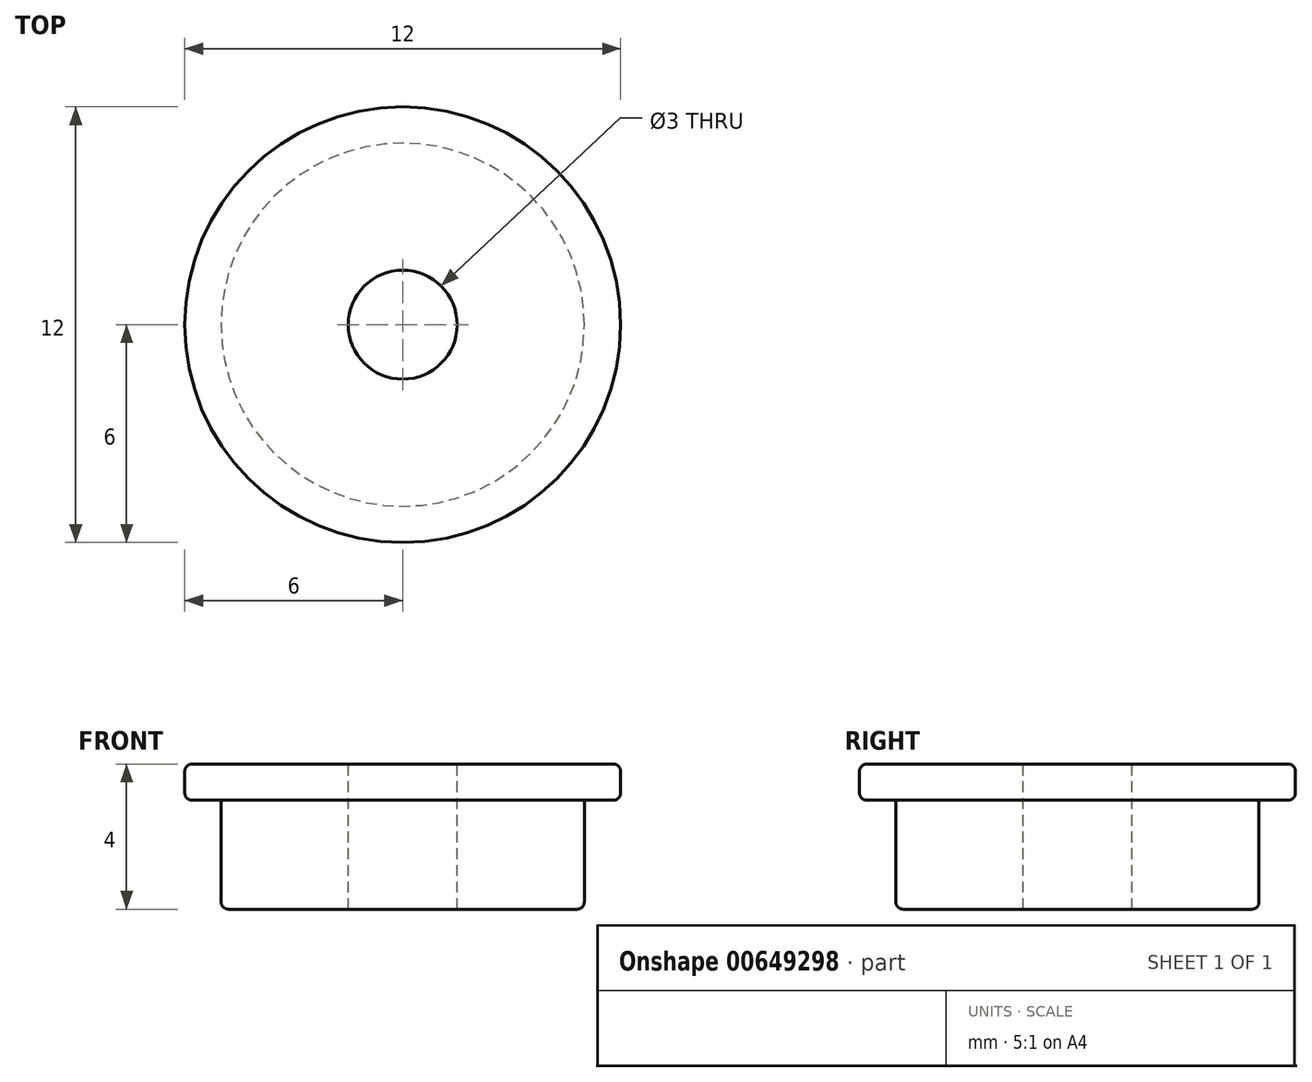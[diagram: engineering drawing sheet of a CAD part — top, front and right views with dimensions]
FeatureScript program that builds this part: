
annotation { "Feature Type Name" : "Feature", "Feature Type Description" : "" }
export const myFeature = defineFeature(function(context is Context, id is Id, definition is map)
    precondition{}
    {
        {
            var Q0;
            Q0=qCreatedBy(makeId("Front.planeOp"),FACE);
            var sketch = newSketch(context, id + "F0", { "sketchPlane" : qUnion([Q0])});
            skLineSegment(sketch, "E0", {"start": v(0, 0) * mm, "end": v(0, 4) * mm});
            skLineSegment(sketch, "E1", {"start": v(0, 4) * mm, "end": v(-5.8, 4) * mm});
            skLineSegment(sketch, "E2", {"start": v(-6, 3.8) * mm, "end": v(-6, 3.2) * mm});
            skLineSegment(sketch, "E3", {"start": v(-5.8, 3) * mm, "end": v(-5, 3) * mm});
            skLineSegment(sketch, "E4", {"start": v(-5, 3) * mm, "end": v(-5, 0.2) * mm});
            skLineSegment(sketch, "E5", {"start": v(-4.8, 0) * mm, "end": v(0, 0) * mm});
            skLineSegment(sketch, "E6", {"start": v(-1.5, 4) * mm, "end": v(-1.5, 0) * mm});
            skPoint(sketch, "E7.visualSharp", {"position": v(-5, 0) * mm});
            skArc(sketch, "E7.filletArc", {"start": v(-5, 0.2) * mm, "mid": v(-4.94, 0.06) * mm, "end": v(-4.8, 0) * mm});
            skPoint(sketch, "E8.visualSharp", {"position": v(-6, 3) * mm});
            skArc(sketch, "E8.filletArc", {"start": v(-6, 3.2) * mm, "mid": v(-5.94, 3.06) * mm, "end": v(-5.8, 3) * mm});
            skPoint(sketch, "E9.visualSharp", {"position": v(-6, 4) * mm});
            skArc(sketch, "E9.filletArc", {"start": v(-5.8, 4) * mm, "mid": v(-5.94, 3.94) * mm, "end": v(-6, 3.8) * mm});
            skArc(sketch, "E10.MirrorCS", {"start": v(-5, -0.2) * mm, "mid": v(-4.94, -0.06) * mm, "end": v(-4.8, 0) * mm});
            skArc(sketch, "E11.MirrorCS", {"start": v(-5.8, -4) * mm, "mid": v(-5.94, -3.94) * mm, "end": v(-6, -3.8) * mm});
            skArc(sketch, "E12.MirrorCS", {"start": v(-6, -3.2) * mm, "mid": v(-5.94, -3.06) * mm, "end": v(-5.8, -3) * mm});
            skPoint(sketch, "E13.MirrorP", {"position": v(-6, -4) * mm});
            skLineSegment(sketch, "E14.MirrorCS", {"start": v(0, 0) * mm, "end": v(0, -4) * mm});
            skPoint(sketch, "E15.MirrorP", {"position": v(-6, -3) * mm});
            skLineSegment(sketch, "E16.MirrorCS", {"start": v(0, -4) * mm, "end": v(-5.8, -4) * mm});
            skLineSegment(sketch, "E17.MirrorCS", {"start": v(-6, -3.8) * mm, "end": v(-6, -3.2) * mm});
            skLineSegment(sketch, "E18.MirrorCS", {"start": v(-5.8, -3) * mm, "end": v(-5, -3) * mm});
            skLineSegment(sketch, "E19.MirrorCS", {"start": v(-5, -3) * mm, "end": v(-5, -0.2) * mm});
            skLineSegment(sketch, "E20.MirrorCS", {"start": v(-1.5, -4) * mm, "end": v(-1.5, 0) * mm});
            skSolve(sketch);
        }
        {
            var Q0;
            Q0=makeQuery(id+"F0.imprint","IMPRINT",FACE,{"disambiguationData":[TD([[makeQuery(id+"F0.imprint","IMPRINT",EDGE,{"derivedFrom":sQuery(id+"F0.wireOp",EDGE,"E2")}),1.0]])]});
            var Q1;
            {var subQ3=sQuery(id+"F0.wireOp",EDGE,"E10.MirrorCS");Q1=makeQuery(id+"F0.imprint","IMPRINT",FACE,{"disambiguationData":[TD([[makeQuery(id+"F0.imprint","IMPRINT",EDGE,{"derivedFrom":subQ3}),-1.0]])]});}
            var Q2;
            Q2=sQuery(id+"F0.wireOp",EDGE,"E14.MirrorCS");
            revolve(context, id + "F1", {"entities" : qUnion([Q0, Q1]), "axis" : qUnion([Q2]), "revolveType" : RevolveType.FULL});
        }
    });
